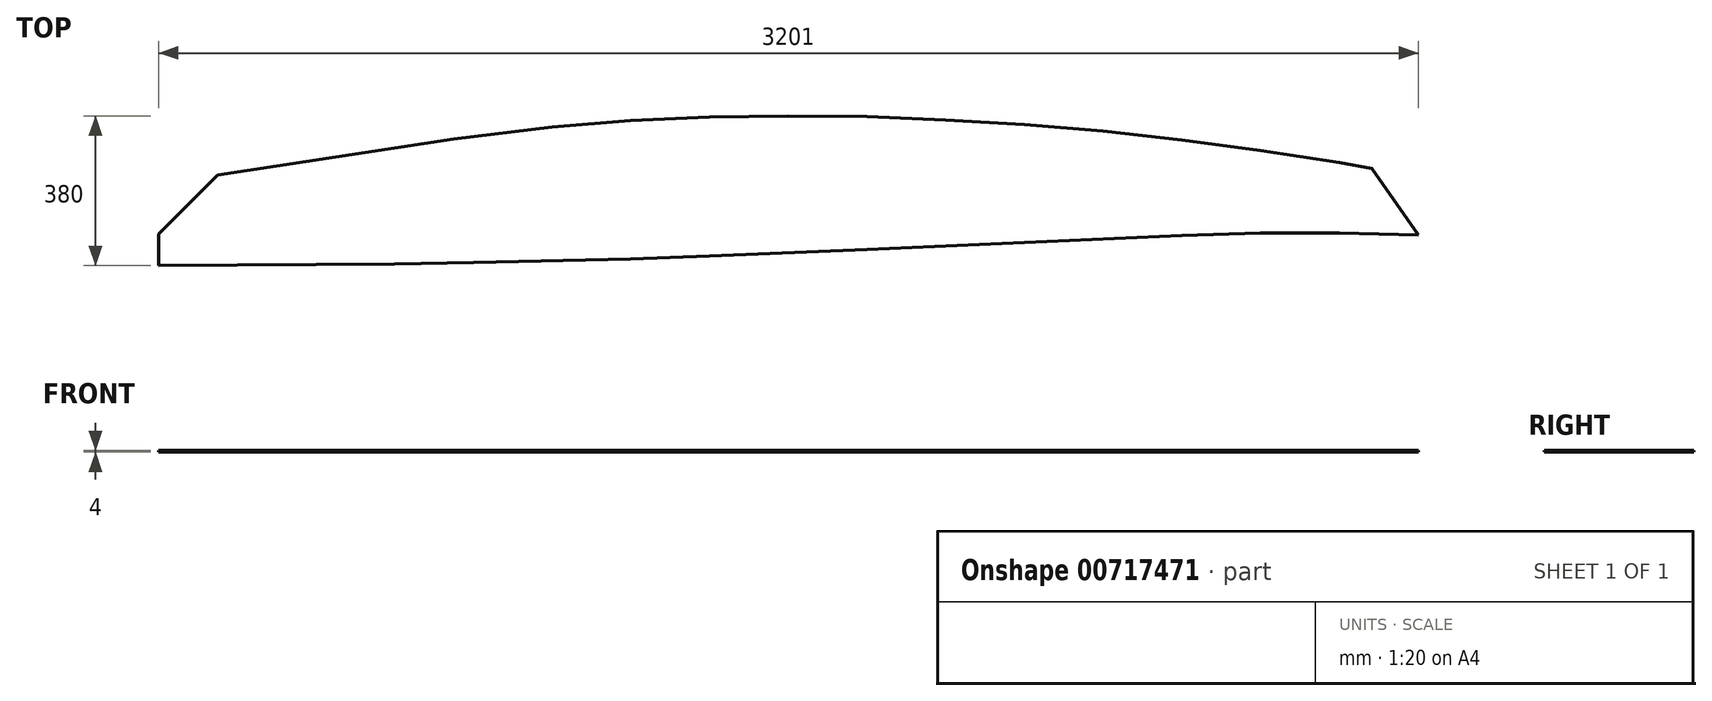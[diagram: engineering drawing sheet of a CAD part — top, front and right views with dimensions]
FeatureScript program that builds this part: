
annotation { "Feature Type Name" : "Feature", "Feature Type Description" : "" }
export const myFeature = defineFeature(function(context is Context, id is Id, definition is map)
    precondition{}
    {
        {
            var Q0;
            Q0=qCreatedBy(makeId("Top.planeOp"),FACE);
            var sketch = newSketch(context, id + "F0", { "sketchPlane" : qUnion([Q0])});
            skLineSegment(sketch, "E0", {"start": v(0, 0) * mm, "end": v(0, 80) * mm});
            skLineSegment(sketch, "E1", {"start": v(150, 230) * mm, "end": v(0, 80) * mm});
            skLineSegment(sketch, "E2", {"start": v(150, 230) * mm, "end": v(750, 321) * mm});
            skLineSegment(sketch, "E3", {"start": v(3083, 246) * mm, "end": v(3201, 77) * mm});
            skLineSegment(sketch, "E4", {"start": v(750, 321) * mm, "end": v(1000, 352) * mm});
            skLineSegment(sketch, "E5", {"start": v(1200, 368) * mm, "end": v(1000, 352) * mm});
            skLineSegment(sketch, "E6", {"start": v(1200, 368) * mm, "end": v(1400, 377) * mm});
            skLineSegment(sketch, "E7", {"start": v(1400, 377) * mm, "end": v(1600, 380) * mm});
            skLineSegment(sketch, "E8", {"start": v(0, 0) * mm, "end": v(4261.7, 0) * mm, "construction": true});
            skLineSegment(sketch, "E9", {"start": v(600, 4) * mm, "end": v(800, 7) * mm});
            skLineSegment(sketch, "E10", {"start": v(800, 7) * mm, "end": v(1000, 12) * mm});
            skLineSegment(sketch, "E11", {"start": v(600, 4) * mm, "end": v(400, 2) * mm});
            skLineSegment(sketch, "E12", {"start": v(400, 2) * mm, "end": v(0, 0) * mm});
            skLineSegment(sketch, "E13", {"start": v(1000, 12) * mm, "end": v(1200, 17) * mm});
            skLineSegment(sketch, "E14", {"start": v(1400, 24) * mm, "end": v(1200, 17) * mm});
            skLineSegment(sketch, "E15", {"start": v(1400, 24) * mm, "end": v(1600, 32) * mm});
            skLineSegment(sketch, "E16", {"start": v(1600, 32) * mm, "end": v(1800, 40) * mm});
            skLineSegment(sketch, "E17", {"start": v(1800, 40) * mm, "end": v(2000, 49) * mm});
            skLineSegment(sketch, "E18", {"start": v(2000, 49) * mm, "end": v(2200, 58) * mm});
            skLineSegment(sketch, "E19", {"start": v(2200, 58) * mm, "end": v(2400, 67) * mm});
            skLineSegment(sketch, "E20", {"start": v(2400, 67) * mm, "end": v(2600, 76) * mm});
            skLineSegment(sketch, "E21", {"start": v(2600, 76) * mm, "end": v(2800, 82) * mm});
            skLineSegment(sketch, "E22", {"start": v(2800, 82) * mm, "end": v(3000, 83) * mm});
            skLineSegment(sketch, "E23", {"start": v(1600, 380) * mm, "end": v(1800, 378) * mm});
            skLineSegment(sketch, "E24", {"start": v(1800, 378) * mm, "end": v(2000, 370) * mm});
            skLineSegment(sketch, "E25", {"start": v(2000, 370) * mm, "end": v(2200, 358) * mm});
            skLineSegment(sketch, "E26", {"start": v(2200, 358) * mm, "end": v(2400, 341) * mm});
            skLineSegment(sketch, "E27", {"start": v(2400, 341) * mm, "end": v(2600, 319) * mm});
            skLineSegment(sketch, "E28", {"start": v(2600, 319) * mm, "end": v(2800, 292) * mm});
            skLineSegment(sketch, "E29", {"start": v(2800, 292) * mm, "end": v(3000, 261) * mm});
            skLineSegment(sketch, "E30", {"start": v(3000, 261) * mm, "end": v(3083, 246) * mm});
            skLineSegment(sketch, "E31", {"start": v(3000, 83) * mm, "end": v(3201, 77) * mm});
            skSolve(sketch);
        }
        {
            var Q0;
            Q0=makeQuery(id+"F0.imprint","IMPRINT",FACE,{"disambiguationData":[TD([[makeQuery(id+"F0.imprint","IMPRINT",EDGE,{"derivedFrom":sQuery(id+"F0.wireOp",EDGE,"E0")}),-1.0]])]});
            extrude(context, id + "F1", {"entities" : qUnion([Q0]), "depth" : 4 * mm, "offsetDistance" : 25 * mm});
        }
    });
